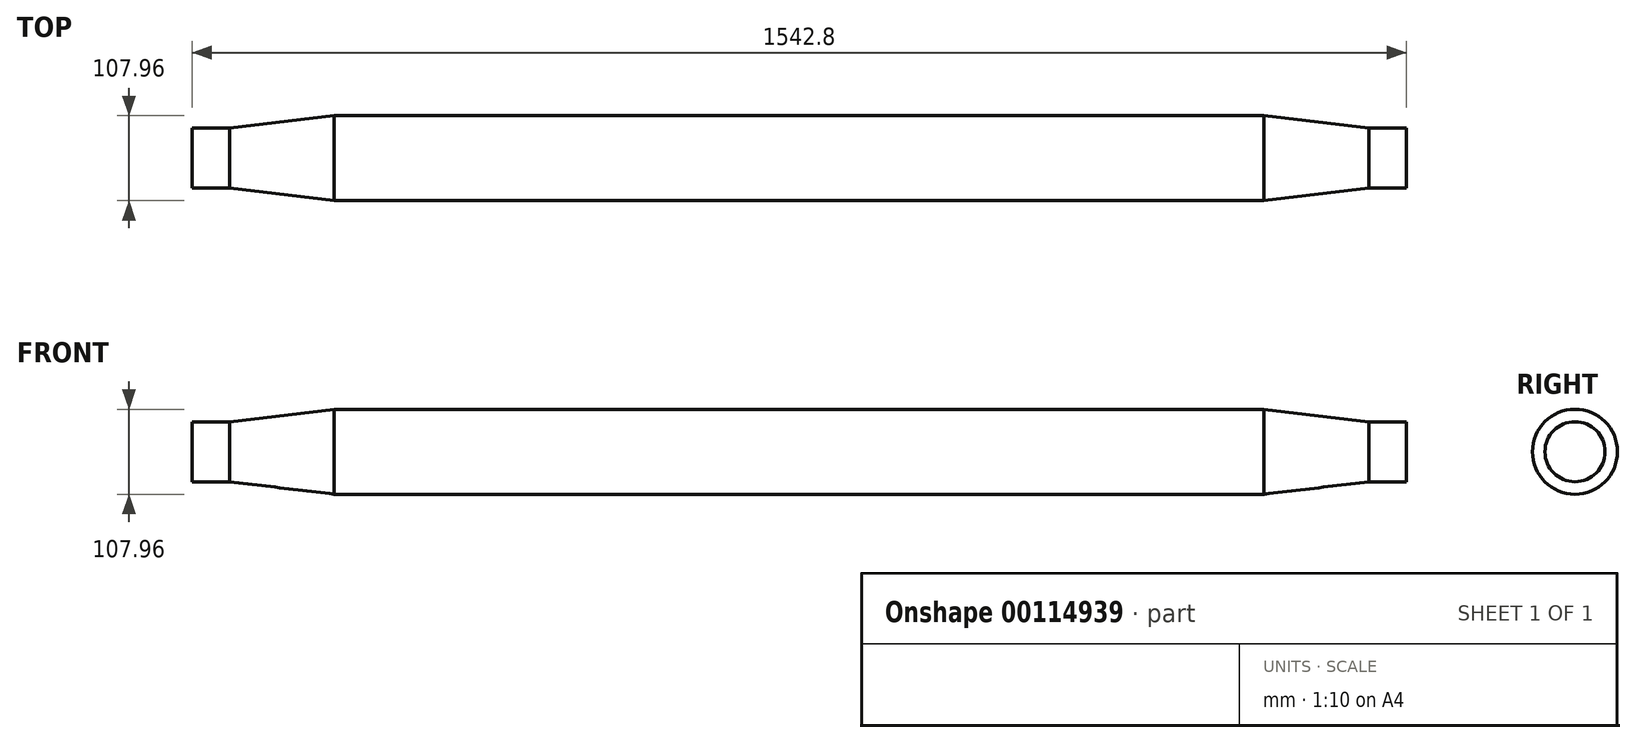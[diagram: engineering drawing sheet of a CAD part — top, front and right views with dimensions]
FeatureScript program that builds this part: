
annotation { "Feature Type Name" : "Feature", "Feature Type Description" : "" }
export const myFeature = defineFeature(function(context is Context, id is Id, definition is map)
    precondition{}
    {
        {
            var Q0;
            Q0=qCreatedBy(makeId("Right.planeOp"),FACE);
            var sketch = newSketch(context, id + "F0", { "sketchPlane" : qUnion([Q0])});
            skCircle(sketch, "E0", {"center": v(0, 0) * mm, "radius": 53.97 * mm});
            skSolve(sketch);
        }
        {
            var Q0;
            Q0=qSketchRegion(id+"F0",true);
            extrude(context, id + "F1", {"entities" : qUnion([Q0]), "endBound" : BoundingType.SYMMETRIC, "depth" : 1181.1 * mm});
        }
        {
            var Q0;
            Q0=makeQuery(id+"F1.opExtrude","CAP_FACE",FACE,{"disambiguationData":[OSD([sQuery(id+"F0.wireOp",EDGE,"E0")])],"isStart":false});
            cPlane(context, id + "F2", {"entities" : qUnion([Q0]), "cplaneType" : CPlaneType.OFFSET, "offset" : 180.85 * mm, "width" : 152.4 * mm, "height" : 152.4 * mm});
        }
        {
            var Q0;
            Q0=qCreatedBy(id+"F2.planeOp",FACE);
            var sketch = newSketch(context, id + "F3", { "sketchPlane" : qUnion([Q0])});
            skCircle(sketch, "E1", {"center": v(0, 0) * mm, "radius": 38.1 * mm});
            skSolve(sketch);
        }
        {
            var Q0;
            Q0=qSketchRegion(id+"F3",true);
            extrude(context, id + "F4", {"entities" : qUnion([Q0]), "oppositeDirection" : true, "depth" : 47.75 * mm});
        }
        {
            var Q0;
            Q0=makeQuery(id+"F4.opExtrude","SWEPT_BODY",BODY,{"disambiguationData":[OSD([sQuery(id+"F3.wireOp",EDGE,"E1")])]});
            var Q1;
            Q1=qCreatedBy(makeId("Right.planeOp"),FACE);
            mirror(context, id + "F5", {"entities" : qUnion([Q0]), "mirrorPlane" : qUnion([Q1])});
        }
        {
            var Q0;
            Q0=makeQuery(id+"F1.opExtrude","CAP_FACE",FACE,{"disambiguationData":[OSD([sQuery(id+"F0.wireOp",EDGE,"E0")])],"isStart":false});
            var Q1;
            Q1=makeQuery(id+"F4.opExtrude","CAP_FACE",FACE,{"disambiguationData":[OSD([sQuery(id+"F3.wireOp",EDGE,"E1")])],"isStart":false});
            loft(context, id + "F6", {"sheetProfilesArray" : [{ "sheetProfileEntities" : qUnion([Q0]) }, { "sheetProfileEntities" : qUnion([Q1]) }]});
        }
        {
            var Q0;
            Q0=makeQuery(id+"F1.opExtrude","CAP_FACE",FACE,{"disambiguationData":[OSD([sQuery(id+"F0.wireOp",EDGE,"E0")])],"isStart":true});
            var Q1;
            Q1=makeQuery(id+"F5.opPattern","COPY",FACE,{"derivedFrom":makeQuery(id+"F4.opExtrude","CAP_FACE",FACE,{"disambiguationData":[OSD([sQuery(id+"F3.wireOp",EDGE,"E1")])],"isStart":false}),"instanceName":"1"});
            loft(context, id + "F7", {"sheetProfilesArray" : [{ "sheetProfileEntities" : qUnion([Q0]) }, { "sheetProfileEntities" : qUnion([Q1]) }]});
        }
    });
